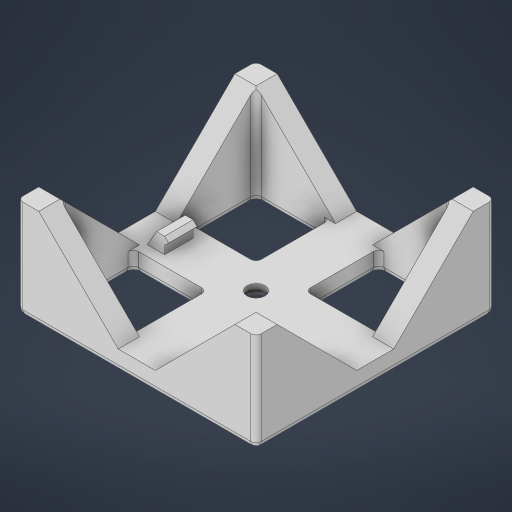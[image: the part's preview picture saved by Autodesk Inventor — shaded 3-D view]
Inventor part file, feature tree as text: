
AUTODESK INVENTOR PART (.ipt)
format: ipt  version: 2023 (Build 270158000, 158)  size: 465,920 bytes
history: native  units: in
note: dims shown in document units (in); Inventor stores cm internally (conversion verified against a paired STEP export)
features: extrude x9, sketch x4, chamfer x2, direct_edit x1, fillet x1, move_body x1
ambient origin geometry x8: Origin, YZ Plane, XZ Plane, XY Plane, X Axis, Y Axis, Z Axis, Center Point
bodies: Solid1 (feature_tree)
feature tree (18):
  extrude  "Extrusion2"  Depth=0.2657in
  extrude  "Extrusion3"  Depth=1.2786in
  extrude  "Extrusion4"  Depth=0.1181in
  extrude  "Extrusion5"  Depth=0.0787in
  extrude  "Extrusion6"  Depth=0.0787in
  extrude  "Extrusion8"  Depth=0.0787in
  extrude  "Extrusion9"  Depth=0.0787in TaperAngle=0.0deg
  extrude  "Extrusion11"  Depth=0.315in
  extrude  "Extrusion12"  Depth=0.315in
  chamfer  "Chamfer2"  Distance=0.315in
  chamfer  "Chamfer3"  Distance=0.315in
  direct_edit  "Direct Edit1"
  fillet  "Fillet1"  Radius=0.315in
  sketch  "Sketch3"  dims[d3=0.5748in d4=0.2657in d11=2.2146in d12=2.2146in]
  sketch  "Sketch4"  dims[d13=1.2587in d14=1.2786in]
  sketch  "Sketch5"  dims[d15=1.2786in d16=0.1181in]
  sketch  "Sketch6"  dims[d17=0.1181in d18=0.1181in d19=0.1181in d20=0.3543in d23=0.2205in d24=0.0in d25=0.315in d26=0.315in d27=0.315in d28=0.315in d29=0.315in d30=0.315in d31=0.315in d32=0.315in d33=1.1811in d34=0.0in d35=0.0354in d36=0.0in d37=0.0236in d38=0.0in d39=0.0118in d40=0.0in d41=3.5433in d42=3.5433in d48=0.3543in d49=45.0deg d50=0.1181in d51=0.0in d52=0.0in d55=45.0deg d56=0.1181in d57=0.0in d58=0.0in d61=0.0157in d62=0.0157in d63=0.0157in d64=0.0157in d65=1.1467in d66=0.2126in d67=0.1181in d68=0.2362in d69=0.0in d70=0.0591in d71=0.0in d72=0.0591in d73=0.0787in d74=45.0deg d75=0.2362in d76=0.0787in d77=30.0deg d78=0.0in d79=0.0in d80=0.063in d84=0.0787in d85=0.0344in d86=0.0197in d87=0.0344in]
  move_body  "Move1"
